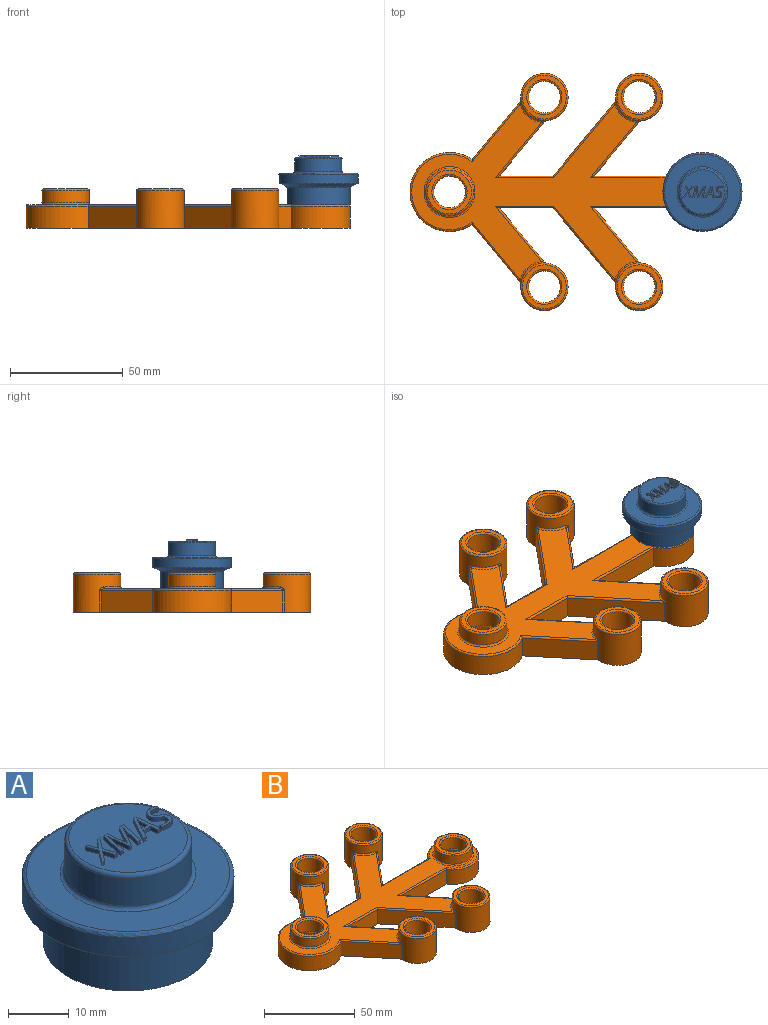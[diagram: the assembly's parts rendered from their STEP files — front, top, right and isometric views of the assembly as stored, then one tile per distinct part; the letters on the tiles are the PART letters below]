
ASSEMBLY  parts=2 mates=1
PART A: 96 faces, bbox 37.9x37.9x21.8 mm
  f0: cylinder r=10.5mm len=17.73mm, axis (0,0,1), area 154.2mm2, adj f12,f19,f94,f95
  f1: cylinder r=10.5mm len=15.36mm, axis (0,0,1), area 154.2mm2, adj f12,f19,f93,f94
  f2: plane 19.6x19.6mm, normal (0,0,1), area 269.7mm2, adj f16,f20,f21,f22,f23,f24,f25,f26
  f3: cylinder r=14mm len=28mm, axis (0,0,1), area 670.5mm2, adj f12,f13
  f4: cone r=14mm half-angle=70deg, axis (0,0,1), area 324.8mm2, adj f5,f13
  f5: cylinder r=17.5mm len=35mm, axis (0,0,1), area 430.3mm2, adj f4,f14
  f6: plane 33.6x33.6mm, normal (0,0,1), area 492.6mm2, adj f14,f15
  f7: cylinder r=10.5mm len=21mm, axis (0,0,1), area 369.5mm2, adj f15,f16
  f8: cone r=0mm half-angle=70deg, axis (0,0,-1), area 76.7mm2, adj f17
  f9: cylinder r=5.25mm len=10.5mm, axis (0,0,1), area 193.3mm2, adj f17,f18
  f10: cone r=10.5mm half-angle=70deg, axis (0,0,-1), area 227.9mm2, adj f18,f19
  f11: cylinder r=10.5mm len=15.36mm, axis (0,0,1), area 154.2mm2, adj f12,f19,f93,f95
  f12: plane 28x28mm, normal (0,0,-1), area 270.3mm2, adj f0,f1,f3,f11,f93,f94,f95
  f13: torus R=14.7mm, axis (0,0,1), area 76.1mm2, adj f3,f4
  f14: torus R=16.8mm, axis (0,0,-1), area 119.1mm2, adj f5,f6
  f15: torus R=11.2mm, axis (0,0,-1), area 74.3mm2, adj f6,f7
  f16: torus R=9.8mm, axis (0,0,-1), area 70.8mm2, adj f2,f7
  f17: torus R=4.55mm, axis (0,0,1), area 27.3mm2, adj f8,f9
  f18: torus R=5.95mm, axis (0,0,-1), area 29.1mm2, adj f9,f10
  f19: torus R=9.8mm, axis (0,0,1), area 53.7mm2, adj f0,f1,f10,f11,f93,f94,f95
  f20: plane 0.78x0.67mm, normal (0,-1,0), area 0.5mm2, adj f2,f21,f31,f32
  f21: plane 2.65x0.96mm, normal (0.94,0.34,0), area 2.2mm2, adj f2,f20,f22,f32
  f22: plane 2.41x1.92mm, normal (0.78,-0.62,0), area 2.4mm2, adj f2,f21,f23,f32
  f23: plane 0.78x0.69mm, normal (0,1,0), area 0.5mm2, adj f2,f22,f24,f32
  f24: plane 1.94x1.51mm, normal (-0.79,0.61,0), area 1.9mm2, adj f2,f23,f25,f32
  f25: plane 1.94x0.78mm, normal (0.94,0.33,0), area 1.6mm2, adj f2,f24,f26,f32
  f26: plane 0.78x0.64mm, normal (0,1,0), area 0.5mm2, adj f2,f25,f27,f32
  f27: plane 2.38x0.9mm, normal (-0.94,-0.35,0), area 2mm2, adj f2,f26,f28,f32
  f28: plane 2.68x2.06mm, normal (-0.79,0.61,0), area 2.6mm2, adj f2,f27,f29,f32
  f29: plane 0.78x0.69mm, normal (0,-1,0), area 0.5mm2, adj f2,f28,f30,f32
  f30: plane 2.19x1.65mm, normal (0.8,-0.6,0), area 2.1mm2, adj f2,f29,f31,f32
  f31: plane 2.19x0.78mm, normal (-0.95,-0.31,0), area 1.8mm2, adj f2,f20,f30,f32
  f32: plane 5.07x4.69mm, normal (0,0,1), area 6.3mm2, adj f20,f21,f22,f23,f24,f25,f26,f27
  f33: plane 4.14x2.25mm, normal (-0.88,0.48,0), area 3.7mm2, adj f2,f34,f50,f51
  f34: plane 0.78x0.03mm, normal (0,1,0), area 0mm2, adj f2,f33,f35,f51
  f35: plane 4.14x0.78mm, normal (0.99,0.12,0), area 3.2mm2, adj f2,f34,f36,f51
  f36: plane 0.89x0.78mm, normal (0,1,0), area 0.7mm2, adj f2,f35,f37,f51
  f37: plane 5.07x1.07mm, normal (-0.98,0.21,0), area 4mm2, adj f2,f36,f38,f51
  f38: plane 0.78x0.6mm, normal (0,-1,0), area 0.5mm2, adj f2,f37,f39,f51
  f39: plane 3.05x0.78mm, normal (0.98,-0.21,0), area 2.4mm2, adj f2,f38,f40,f51
  f40: extruded ~1.4x0.78mm, area 1.1mm2, adj f2,f39,f41,f51
  f41: plane 0.78x0.03mm, normal (0,-1,0), area 0mm2, adj f2,f40,f42,f51
  f42: plane 4.44x0.78mm, normal (-0.99,-0.12,0), area 3.5mm2, adj f2,f41,f43,f51
  f43: plane 0.78x0.5mm, normal (0,-1,0), area 0.4mm2, adj f2,f42,f44,f51
  f44: plane 4.45x2.44mm, normal (0.88,-0.48,0), area 3.9mm2, adj f2,f43,f45,f51
  f45: plane 0.78x0.01mm, normal (0,-1,0), area 0mm2, adj f2,f44,f46,f51
  f46: extruded ~1.44x0.78mm, area 1.2mm2, adj f2,f45,f47,f51
  f47: plane 3.01x0.78mm, normal (-0.98,0.21,0), area 2.4mm2, adj f2,f46,f48,f51
  f48: plane 0.78x0.64mm, normal (0,-1,0), area 0.5mm2, adj f2,f47,f49,f51
  f49: plane 5.07x1.05mm, normal (0.98,-0.2,0), area 4mm2, adj f2,f48,f50,f51
  f50: plane 0.97x0.78mm, normal (0,1,0), area 0.8mm2, adj f2,f33,f49,f51
  f51: plane 5.71x5.07mm, normal (0,0,1), area 11.3mm2, adj f33,f34,f35,f36,f37,f38,f39,f40
  f52: plane 1.06x0.78mm, normal (-0.99,-0.11,0), area 0.8mm2, adj f53,f64,f65,f66
  f53: plane 1.34x0.78mm, normal (0,1,0), area 1mm2, adj f52,f54,f65,f66
  f54: extruded ~1.72x0.89mm, area 1.5mm2, adj f53,f55,f65,f66
  f55: extruded ~0.78x0.54mm, area 0.5mm2, adj f54,f64,f65,f66
  f56: plane 1.71x0.78mm, normal (0,-1,0), area 1.3mm2, adj f2,f57,f63,f65
  f57: plane 1.58x0.78mm, normal (-0.99,-0.12,0), area 1.2mm2, adj f2,f56,f58,f65
  f58: plane 0.78x0.63mm, normal (0,-1,0), area 0.5mm2, adj f2,f57,f59,f65
  f59: plane 5.07x0.78mm, normal (0.99,0.12,0), area 4mm2, adj f2,f58,f60,f65
  f60: plane 0.78x0.67mm, normal (0,1,0), area 0.5mm2, adj f2,f59,f61,f65
  f61: plane 5.07x2.75mm, normal (-0.88,0.48,0), area 4.5mm2, adj f2,f60,f62,f65
  f62: plane 0.78x0.7mm, normal (0,-1,0), area 0.5mm2, adj f2,f61,f63,f65
  f63: plane 1.58x0.82mm, normal (0.89,-0.46,0), area 1.4mm2, adj f2,f56,f62,f65
  f64: extruded ~1.19x0.78mm, area 0.9mm2, adj f52,f55,f65,f66
  f65: plane 5.07x4.05mm, normal (0,0,1), area 7mm2, adj f52,f53,f54,f55,f56,f57,f58,f59
  f66: plane 2.25x1.34mm, normal (0,0,1), area 1.4mm2, adj f52,f53,f54,f55,f64
  f67: extruded ~1.13x0.78mm, area 1mm2, adj f2,f68,f91,f92
  f68: extruded ~0.78x0.49mm, area 0.4mm2, adj f2,f67,f69,f92
  f69: extruded ~0.78x0.39mm, area 0.4mm2, adj f2,f68,f70,f92
  f70: extruded ~0.78x0.67mm, area 0.6mm2, adj f2,f69,f71,f92
  f71: extruded ~0.78x0.59mm, area 0.6mm2, adj f2,f70,f72,f92
  f72: extruded ~0.78x0.45mm, area 0.4mm2, adj f2,f71,f73,f92
  f73: extruded ~0.78x0.63mm, area 0.6mm2, adj f2,f72,f74,f92
  f74: extruded ~0.78x0.72mm, area 0.6mm2, adj f2,f73,f75,f92
  f75: extruded ~0.78x0.53mm, area 0.4mm2, adj f2,f74,f76,f92
  f76: extruded ~0.78x0.5mm, area 0.4mm2, adj f2,f75,f77,f92
  f77: plane 0.78x0.54mm, normal (0.91,-0.41,0), area 0.5mm2, adj f2,f76,f78,f92
  f78: extruded ~1.27x0.78mm, area 1mm2, adj f2,f77,f79,f92
  f79: extruded ~0.86x0.78mm, area 0.7mm2, adj f2,f78,f80,f92
  f80: extruded ~0.78x0.6mm, area 0.6mm2, adj f2,f79,f81,f92
  f81: extruded ~0.78x0.77mm, area 0.6mm2, adj f2,f80,f82,f92
  f82: extruded ~0.78x0.69mm, area 0.6mm2, adj f2,f81,f83,f92
  f83: extruded ~0.78x0.72mm, area 0.7mm2, adj f2,f82,f84,f92
  f84: extruded ~0.78x0.67mm, area 0.6mm2, adj f2,f83,f85,f92
  f85: extruded ~0.78x0.46mm, area 0.4mm2, adj f2,f84,f86,f92
  f86: extruded ~0.78x0.69mm, area 0.6mm2, adj f2,f85,f87,f92
  f87: extruded ~0.86x0.78mm, area 0.7mm2, adj f2,f86,f88,f92
  f88: extruded ~1.19x0.78mm, area 1mm2, adj f2,f87,f89,f92
  f89: plane 0.78x0.62mm, normal (-1,0,0), area 0.5mm2, adj f2,f88,f90,f92
  f90: extruded ~1.18x0.78mm, area 0.9mm2, adj f2,f89,f91,f92
  f91: extruded ~1.37x0.78mm, area 1.1mm2, adj f2,f67,f90,f92
  f92: plane 5.21x3.55mm, normal (0,0,1), area 5.9mm2, adj f67,f68,f69,f70,f71,f72,f73,f74
  f93: cylinder r=0.44mm len=7.95mm, axis (0,0,-1), area 10.6mm2, adj f1,f11,f12,f19
  f94: cylinder r=0.44mm len=7.95mm, axis (0,0,-1), area 10.6mm2, adj f0,f1,f12,f19
  f95: cylinder r=0.44mm len=7.95mm, axis (0,0,-1), area 10.6mm2, adj f0,f11,f12,f19
PART B: 137 faces, bbox 146.1x106.7x17.5 mm
  f0: plane 91.42x1.75mm, normal (0,1,0), area 151.8mm2, adj f1,f2,f3,f127,f128,f130,f131,f133
  f1: cylinder r=10.55mm len=9.78mm, axis (0,0,-1), area 46mm2, adj f0,f3,f12,f116,f117,f121,f122,f135
  f2: cylinder r=10.55mm len=9.78mm, axis (0,0,-1), area 46mm2, adj f0,f3,f19,f113,f114,f121,f122,f135
  f3: plane 143.5x105mm, normal (0,0,-1), area 4302.8mm2, adj f0,f1,f2,f4,f5,f8,f10,f13
  f4: cylinder r=10.55mm len=9.78mm, axis (0,0,-1), area 59.3mm2, adj f3,f9,f119,f120
  f5: cylinder r=10.55mm len=8.47mm, axis (0,0,-1), area 59.3mm2, adj f3,f7,f115,f120
  f6: cone r=10.5mm half-angle=45deg, axis (0,0,-1), area 270mm2, adj f7,f9,f11,f12,f14,f57,f58,f115
  f7: plane 8.48x4.92mm, normal (0,0,-1), area 0.5mm2, adj f5,f6,f115,f120
  f8: cylinder r=10.55mm len=8.47mm, axis (0,0,-1), area 59.3mm2, adj f3,f57,f118,f119
  f9: plane 9.78x1.25mm, normal (0,0,-1), area 0.5mm2, adj f4,f6,f119,f120
  f10: cylinder r=10.55mm len=8.47mm, axis (0,0,-1), area 59.3mm2, adj f3,f11,f117,f118
  f11: plane 8.48x4.92mm, normal (0,0,-1), area 0.5mm2, adj f6,f10,f117,f118
  f12: plane 9.78x1.25mm, normal (0,0,-1), area 0.5mm2, adj f1,f6,f116,f117
  f13: cylinder r=10.55mm len=8.47mm, axis (0,0,-1), area 59.3mm2, adj f3,f14,f115,f116
  f14: plane 8.48x4.92mm, normal (0,0,-1), area 0.5mm2, adj f6,f13,f115,f116
  f15: cylinder r=10.55mm len=8.47mm, axis (0,0,-1), area 59.3mm2, adj f3,f17,f109,f114
  f16: cone r=10.5mm half-angle=45deg, axis (0,0,-1), area 270mm2, adj f17,f19,f21,f23,f25,f53,f54,f109
  f17: plane 8.48x4.92mm, normal (0,0,-1), area 0.5mm2, adj f15,f16,f109,f114
  f18: cylinder r=10.55mm len=8.47mm, axis (0,0,-1), area 59.3mm2, adj f3,f53,f112,f113
  f19: plane 9.78x1.25mm, normal (0,0,-1), area 0.5mm2, adj f2,f16,f113,f114
  f20: cylinder r=10.55mm len=8.47mm, axis (0,0,-1), area 59.3mm2, adj f3,f21,f111,f112
  f21: plane 8.48x4.92mm, normal (0,0,-1), area 0.5mm2, adj f16,f20,f111,f112
  f22: cylinder r=10.55mm len=9.78mm, axis (0,0,-1), area 59.3mm2, adj f3,f23,f110,f111
  f23: plane 9.78x1.25mm, normal (0,0,-1), area 0.5mm2, adj f16,f22,f110,f111
  f24: cylinder r=10.55mm len=8.47mm, axis (0,0,-1), area 59.3mm2, adj f3,f25,f109,f110
  f25: plane 8.48x4.92mm, normal (0,0,-1), area 0.5mm2, adj f16,f24,f109,f110
  f26: plane 24.25x20.13mm, normal (0.77,0.64,0), area 306.4mm2, adj f3,f27,f92,f94
  f27: plane 23.8x9.72mm, normal (0,-1,0), area 231.4mm2, adj f3,f26,f28,f90
  f28: plane 33.19x27.56mm, normal (-0.77,-0.64,0), area 419.4mm2, adj f3,f27,f83,f88
  f29: cylinder r=10.5mm len=21mm, axis (0,0,-1), area 924.3mm2, adj f3,f78,f80,f82,f83,f85,f106
  f30: plane 24.25x20.13mm, normal (0.77,0.64,0), area 306.4mm2, adj f3,f31,f77,f78
  f31: plane 35.84x9.72mm, normal (0,-1,0), area 348.5mm2, adj f3,f30,f32,f74
  f32: cylinder r=14mm len=28mm, axis (0,0,-1), area 712.7mm2, adj f3,f31,f33,f72
  f33: plane 35.84x9.72mm, normal (0,1,0), area 348.5mm2, adj f3,f32,f34,f69
  f34: plane 24.25x20.13mm, normal (0.77,-0.64,0), area 306.4mm2, adj f3,f33,f63,f67
  f35: cylinder r=10.5mm len=21mm, axis (0,0,-1), area 924.3mm2, adj f3,f61,f62,f63,f64,f65,f103
  f36: plane 33.19x27.56mm, normal (-0.77,0.64,0), area 419.4mm2, adj f3,f37,f61,f66
  f37: plane 23.8x9.72mm, normal (0,1,0), area 231.4mm2, adj f3,f36,f38,f68
  f38: plane 24.25x20.13mm, normal (0.77,-0.64,0), area 306.4mm2, adj f3,f37,f70,f71
  f39: cylinder r=10.5mm len=21mm, axis (0,0,-1), area 924.3mm2, adj f3,f70,f73,f75,f76,f79,f101
  f40: plane 25.81x21.43mm, normal (-0.77,0.64,0), area 326.1mm2, adj f3,f41,f75,f81
  f41: cylinder r=17.5mm len=35mm, axis (0,0,-1), area 740.7mm2, adj f3,f40,f42,f84
  f42: plane 25.81x21.43mm, normal (-0.77,-0.64,0), area 326.1mm2, adj f3,f41,f86,f87
  f43: cylinder r=7mm len=16.72mm, axis (0,0,-1), area 735.5mm2, adj f3,f105
  f44: cylinder r=7mm len=16.72mm, axis (0,0,-1), area 735.5mm2, adj f3,f100
  f45: cylinder r=7mm len=16.72mm, axis (0,0,-1), area 735.5mm2, adj f3,f104
  f46: cylinder r=7mm len=16.72mm, axis (0,0,-1), area 735.5mm2, adj f3,f102
  f47: cylinder r=10.5mm len=21mm, axis (0,0,-1), area 924.3mm2, adj f3,f86,f89,f91,f93,f94,f99
  f48: plane 141.94x77.48mm, normal (0,0,1), area 3356.7mm2, adj f62,f66,f67,f68,f69,f71,f72,f74
  f49: plane 19.44x19.44mm, normal (0,0,1), area 106.9mm2, adj f105,f106
  f50: plane 19.44x19.44mm, normal (0,0,1), area 106.9mm2, adj f103,f104
  f51: plane 19.44x19.44mm, normal (0,0,1), area 106.9mm2, adj f101,f102
  f52: plane 19.44x19.44mm, normal (0,0,1), area 106.9mm2, adj f99,f100
  f53: plane 8.48x4.92mm, normal (0,0,-1), area 0.5mm2, adj f16,f18,f112,f113
  f54: cylinder r=7mm len=14mm, axis (0,0,-1), area 325mm2, adj f16,f108
  f55: cylinder r=10.5mm len=21mm, axis (0,0,-1), area 359.2mm2, adj f95,f107
  f56: plane 19.44x19.44mm, normal (0,0,1), area 106.9mm2, adj f107,f108
  f57: plane 8.48x4.92mm, normal (0,0,-1), area 0.5mm2, adj f6,f8,f118,f119
  f58: cylinder r=7mm len=14mm, axis (0,0,-1), area 325mm2, adj f6,f98
  f59: cylinder r=10.5mm len=21mm, axis (0,0,-1), area 359.2mm2, adj f96,f97
  f60: plane 19.44x19.44mm, normal (0,0,1), area 106.9mm2, adj f97,f98
  f61: cylinder r=0.78mm len=9.72mm, axis (0,0,-1), area 6.1mm2, adj f3,f35,f36,f64
  f62: torus R=11.28mm, axis (0,0,1), area 15.4mm2, adj f35,f48,f64,f65
  f63: cylinder r=0.78mm len=9.72mm, axis (0,0,-1), area 6.1mm2, adj f3,f34,f35,f65
  f64: bspline ~2.17x1.84mm, area 1.9mm2, adj f35,f61,f62,f66
  f65: bspline ~2.34x1.79mm, area 1.9mm2, adj f35,f62,f63,f67
  f66: cylinder r=0.78mm len=33.97mm, axis (0.64,0.77,0), area 52.3mm2, adj f36,f48,f64,f68
  f67: cylinder r=0.78mm len=26.02mm, axis (-0.64,-0.77,0), area 38.7mm2, adj f34,f48,f65,f69
  f68: cylinder r=0.78mm len=25.82mm, axis (1,0,0), area 30mm2, adj f37,f48,f66,f71
  f69: cylinder r=0.78mm len=37.96mm, axis (1,0,0), area 44.7mm2, adj f33,f48,f67,f72
  f70: cylinder r=0.78mm len=9.72mm, axis (0,0,-1), area 6.1mm2, adj f3,f38,f39,f73
  f71: cylinder r=0.78mm len=26.02mm, axis (-0.64,-0.77,0), area 38.7mm2, adj f38,f48,f68,f73
  f72: torus R=13.22mm, axis (0,0,1), area 88.1mm2, adj f32,f48,f69,f74
  f73: bspline ~2.34x1.79mm, area 1.9mm2, adj f39,f70,f71,f76
  f74: cylinder r=0.78mm len=37.96mm, axis (-1,0,0), area 44.7mm2, adj f31,f48,f72,f77
  f75: cylinder r=0.78mm len=9.72mm, axis (0,0,-1), area 6.1mm2, adj f3,f39,f40,f79
  f76: torus R=11.28mm, axis (0,0,1), area 15.4mm2, adj f39,f48,f73,f79
  f77: cylinder r=0.78mm len=26.02mm, axis (0.64,-0.77,0), area 38.7mm2, adj f30,f48,f74,f80
  f78: cylinder r=0.78mm len=9.72mm, axis (0,0,-1), area 6.1mm2, adj f3,f29,f30,f80
  f79: bspline ~2.17x1.84mm, area 1.9mm2, adj f39,f75,f76,f81
  f80: bspline ~2.06x1.84mm, area 1.9mm2, adj f29,f77,f78,f82
  f81: cylinder r=0.78mm len=26.86mm, axis (0.64,0.77,0), area 40.7mm2, adj f40,f48,f79,f84
  f82: torus R=11.28mm, axis (0,0,1), area 15.4mm2, adj f29,f48,f80,f85
  f83: cylinder r=0.78mm len=9.72mm, axis (0,0,-1), area 6.1mm2, adj f3,f28,f29,f85
  f84: torus R=16.72mm, axis (0,0,1), area 92.2mm2, adj f41,f48,f81,f87
  f85: bspline ~2.4x1.79mm, area 1.9mm2, adj f29,f82,f83,f88
  f86: cylinder r=0.78mm len=9.72mm, axis (0,0,-1), area 6.1mm2, adj f3,f42,f47,f89
  f87: cylinder r=0.78mm len=26.86mm, axis (-0.64,0.77,0), area 40.7mm2, adj f42,f48,f84,f89
  f88: cylinder r=0.78mm len=33.97mm, axis (-0.64,0.77,0), area 52.3mm2, adj f28,f48,f85,f90
  f89: bspline ~2.4x1.79mm, area 1.9mm2, adj f47,f86,f87,f91
  f90: cylinder r=0.78mm len=25.82mm, axis (-1,0,0), area 30mm2, adj f27,f48,f88,f92
  f91: torus R=11.28mm, axis (0,0,1), area 15.4mm2, adj f47,f48,f89,f93
  f92: cylinder r=0.78mm len=26.02mm, axis (0.64,-0.77,0), area 38.7mm2, adj f26,f48,f90,f93
  f93: bspline ~2.06x1.84mm, area 1.9mm2, adj f47,f91,f92,f94
  f94: cylinder r=0.78mm len=9.72mm, axis (0,0,-1), area 6.1mm2, adj f3,f26,f47,f93
  f95: torus R=11.28mm, axis (0,0,1), area 82.8mm2, adj f48,f55
  f96: torus R=11.28mm, axis (0,0,1), area 82.8mm2, adj f48,f59
  f97: torus R=9.72mm, axis (0,0,1), area 78.4mm2, adj f59,f60
  f98: torus R=7.78mm, axis (0,0,1), area 55.9mm2, adj f58,f60
  f99: torus R=9.72mm, axis (0,0,1), area 78.4mm2, adj f47,f52
  f100: torus R=7.78mm, axis (0,0,1), area 55.9mm2, adj f44,f52
  f101: torus R=9.72mm, axis (0,0,1), area 78.4mm2, adj f39,f51
  f102: torus R=7.78mm, axis (0,0,1), area 55.9mm2, adj f46,f51
  f103: torus R=9.72mm, axis (0,0,1), area 78.4mm2, adj f35,f50
  f104: torus R=7.78mm, axis (0,0,1), area 55.9mm2, adj f45,f50
  f105: torus R=7.78mm, axis (0,0,1), area 55.9mm2, adj f43,f49
  f106: torus R=9.72mm, axis (0,0,1), area 78.4mm2, adj f29,f49
  f107: torus R=9.72mm, axis (0,0,1), area 78.4mm2, adj f55,f56
  f108: torus R=7.78mm, axis (0,0,1), area 55.9mm2, adj f54,f56
  f109: cylinder r=0.44mm len=6.22mm, axis (0,0,-1), area 8.2mm2, adj f3,f15,f16,f17,f24,f25
  f110: cylinder r=0.44mm len=6.22mm, axis (0,0,-1), area 8.2mm2, adj f3,f16,f22,f23,f24,f25
  f111: cylinder r=0.44mm len=6.22mm, axis (0,0,-1), area 8.2mm2, adj f3,f16,f20,f21,f22,f23
  f112: cylinder r=0.44mm len=6.22mm, axis (0,0,-1), area 8.2mm2, adj f3,f16,f18,f20,f21,f53
  f113: cylinder r=0.44mm len=6.22mm, axis (0,0,-1), area 8.2mm2, adj f2,f3,f16,f18,f19,f53
  f114: cylinder r=0.44mm len=6.22mm, axis (0,0,-1), area 8.2mm2, adj f2,f3,f15,f16,f17,f19
  f115: cylinder r=0.44mm len=6.22mm, axis (0,0,-1), area 8.2mm2, adj f3,f5,f6,f7,f13,f14
  f116: cylinder r=0.44mm len=6.22mm, axis (0,0,-1), area 8.2mm2, adj f1,f3,f6,f12,f13,f14
  f117: cylinder r=0.44mm len=6.22mm, axis (0,0,-1), area 8.2mm2, adj f1,f3,f6,f10,f11,f12
  f118: cylinder r=0.44mm len=6.22mm, axis (0,0,-1), area 8.2mm2, adj f3,f6,f8,f10,f11,f57
  f119: cylinder r=0.44mm len=6.22mm, axis (0,0,-1), area 8.2mm2, adj f3,f4,f6,f8,f9,f57
  f120: cylinder r=0.44mm len=6.22mm, axis (0,0,-1), area 8.2mm2, adj f3,f4,f5,f6,f7,f9
  f121: plane 91.42x1.75mm, normal (0,-1,0), area 155.9mm2, adj f1,f2,f3,f123,f125,f126,f135
  f122: plane 90.93x1.17mm, normal (0,0,-1), area 106.1mm2, adj f1,f2,f135,f136
  f123: plane 2.92x1.4mm, normal (-1,0,0), area 4.1mm2, adj f3,f121,f124,f126
  f124: plane 2.92x1.4mm, normal (0,-1,0), area 4.1mm2, adj f3,f123,f125,f126
  f125: plane 2.92x1.4mm, normal (1,0,0), area 4.1mm2, adj f3,f121,f124,f126
  f126: plane 2.92x2.92mm, normal (0,0,1), area 8.5mm2, adj f121,f123,f124,f125
  f127: plane 2.92x1.4mm, normal (-1,0,0), area 4.1mm2, adj f0,f3,f129,f130
  f128: plane 2.92x1.4mm, normal (1,0,0), area 4.1mm2, adj f0,f3,f129,f130
  f129: plane 2.92x1.4mm, normal (0,1,0), area 4.1mm2, adj f3,f127,f128,f130
  f130: plane 2.92x2.92mm, normal (0,0,1), area 8.5mm2, adj f0,f127,f128,f129
  f131: plane 2.92x1.4mm, normal (1,0,0), area 4.1mm2, adj f0,f3,f132,f134
  f132: plane 2.92x1.4mm, normal (0,1,0), area 4.1mm2, adj f3,f131,f133,f134
  f133: plane 2.92x1.4mm, normal (-1,0,0), area 4.1mm2, adj f0,f3,f132,f134
  f134: plane 2.92x2.92mm, normal (0,0,1), area 8.5mm2, adj f0,f131,f132,f133
  f135: plane 91.43x1.76mm, normal (0,-0.71,-0.71), area 225.5mm2, adj f1,f2,f121,f122
  f136: plane 91.43x1.76mm, normal (0,0.71,-0.71), area 225.5mm2, adj f0,f1,f2,f122
PLACE A t=(74.38,-5.75,10.5)mm
PLACE B at identity
MATE fastened A.f15 <-> B.f2  axis (0,0,-1) through (74.38,-5.75,10.5)mm
